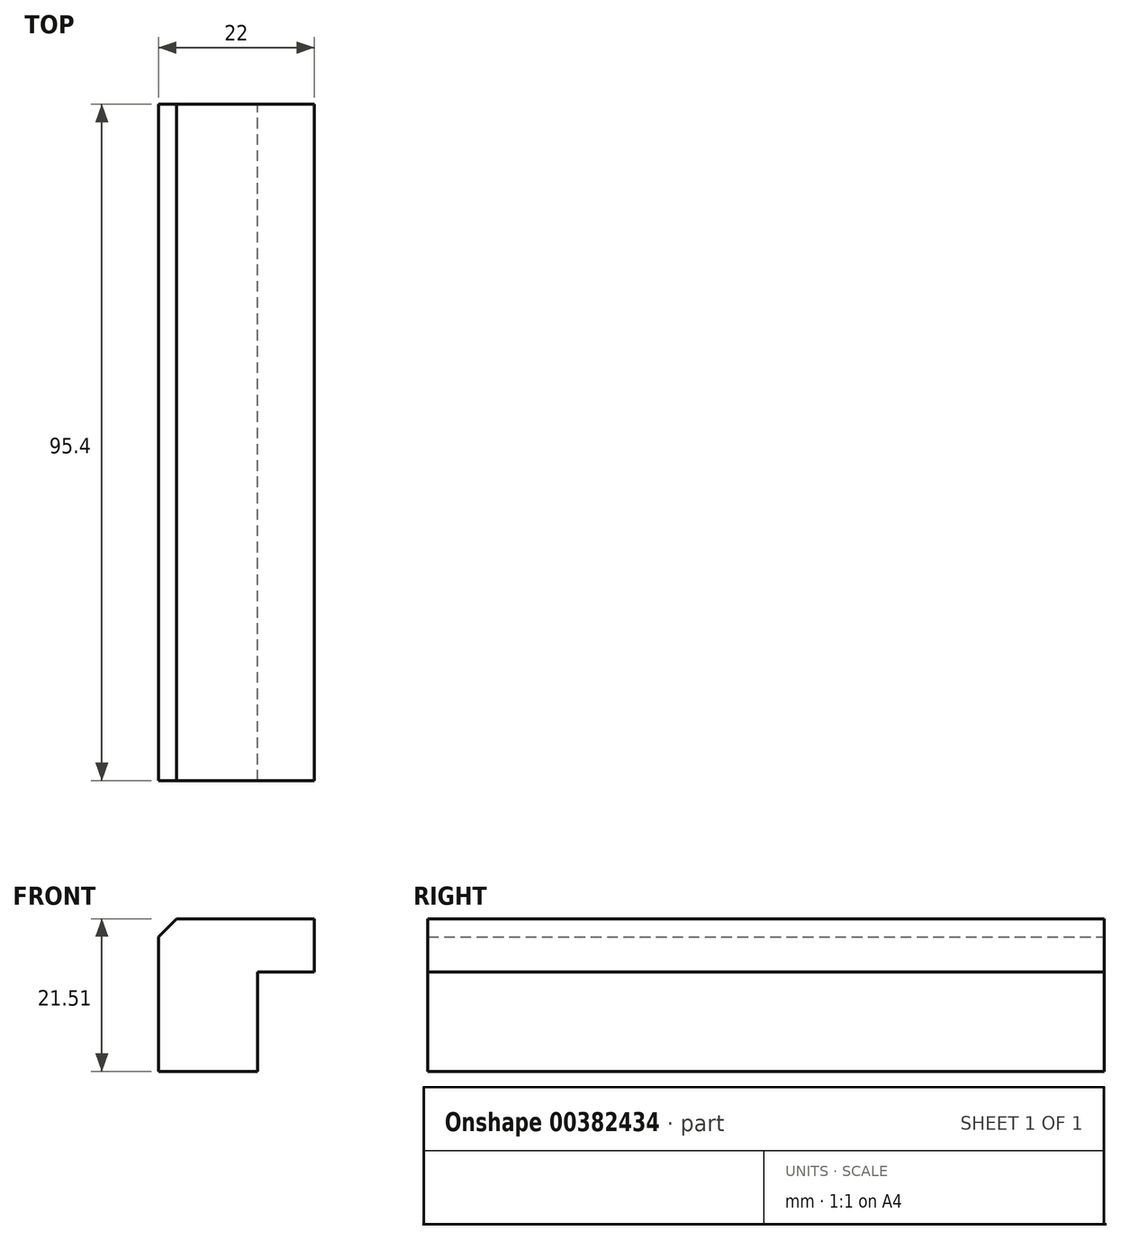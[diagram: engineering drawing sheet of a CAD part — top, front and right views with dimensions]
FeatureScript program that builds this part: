
annotation { "Feature Type Name" : "Feature", "Feature Type Description" : "" }
export const myFeature = defineFeature(function(context is Context, id is Id, definition is map)
    precondition{}
    {
        {
            var Q0;
            Q0=qCreatedBy(makeId("Front.planeOp"),FACE);
            var sketch = newSketch(context, id + "F0", { "sketchPlane" : qUnion([Q0])});
            skLineSegment(sketch, "E0", {"start": v(-34.55, 16.47) * mm, "end": v(-20.55, 16.47) * mm});
            skLineSegment(sketch, "E1", {"start": v(-20.55, 16.47) * mm, "end": v(-20.55, 30.47) * mm});
            skLineSegment(sketch, "E2", {"start": v(-20.55, 30.47) * mm, "end": v(-12.55, 30.47) * mm});
            skLineSegment(sketch, "E3", {"start": v(-12.55, 30.47) * mm, "end": v(-12.55, 37.98) * mm});
            skLineSegment(sketch, "E4", {"start": v(-12.55, 37.98) * mm, "end": v(-34.55, 37.98) * mm});
            skLineSegment(sketch, "E5", {"start": v(-34.55, 37.98) * mm, "end": v(-34.55, 16.47) * mm});
            skSolve(sketch);
        }
        {
            var Q0;
            Q0 = qSketchRegion(id + "F0", true);
            extrude(context, id + "F1", {"entities" : qUnion([Q0]), "depth" : 25.4 * mm});
        }
        {
            var Q0;
            Q0=makeQuery(id+"F1.opExtrude","SWEPT_EDGE",EDGE,{"disambiguationData":[OSD([sQuery(id+"F0.wireOp",EDGE,"E4"),sQuery(id+"F0.wireOp",EDGE,"E5")])]});
            chamfer(context, id + "F2", {"entities" : qUnion([Q0]), "width" : 2.54 * mm, "tangentPropagation" : true});
        }
        {
            var Q0;
            Q0=makeQuery(id+"F1.opExtrude","CAP_FACE",FACE,{"disambiguationData":[OSD([sQuery(id+"F0.wireOp",EDGE,"E0"),sQuery(id+"F0.wireOp",EDGE,"E1"),sQuery(id+"F0.wireOp",EDGE,"E2"),sQuery(id+"F0.wireOp",EDGE,"E3"),sQuery(id+"F0.wireOp",EDGE,"E4"),sQuery(id+"F0.wireOp",EDGE,"E5")])],"isStart":true});
            extrude(context, id + "F3", {"entities" : qUnion([Q0]), "operationType" : NewBodyOperationType.ADD, "depth" : 70 * mm});
        }
    });
